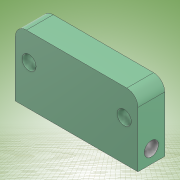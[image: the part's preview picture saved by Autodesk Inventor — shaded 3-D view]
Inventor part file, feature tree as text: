
AUTODESK INVENTOR PART (.ipt)
format: ipt  version: 2022 (Build 260153000, 153)  size: 151,040 bytes
history: native  units: mm
features: extrude x3, sketch x3, other x1, fillet x1
ambient origin geometry x8: Origin, YZ Plane, XZ Plane, XY Plane, X Axis, Y Axis, Z Axis, Center Point
bodies: Body1 (feature_tree)
feature tree (8):
  other  "Sólido1"
  extrude  "Extrusión1"  Depth=55.0mm
  fillet  "Empalme1"  Radius=20.0mm
  extrude  "Extrusión5"  Depth=5.0mm
  extrude  "Extrusión6"  Depth=10.0mm TaperAngle=0.0deg
  sketch  "Boceto1"  dims[d0=6.35mm d1=55.0mm d3=20.0mm]
  sketch  "Boceto7"  dims[d4=12.0mm d5=0.0mm d15=5.0mm]
  sketch  "Boceto8"  dims[d23=42.67mm d24=10.0mm d25=0.0mm d26=6.35mm d27=6.0mm d29=55.0mm d30=0.0mm d31=8.0mm]
